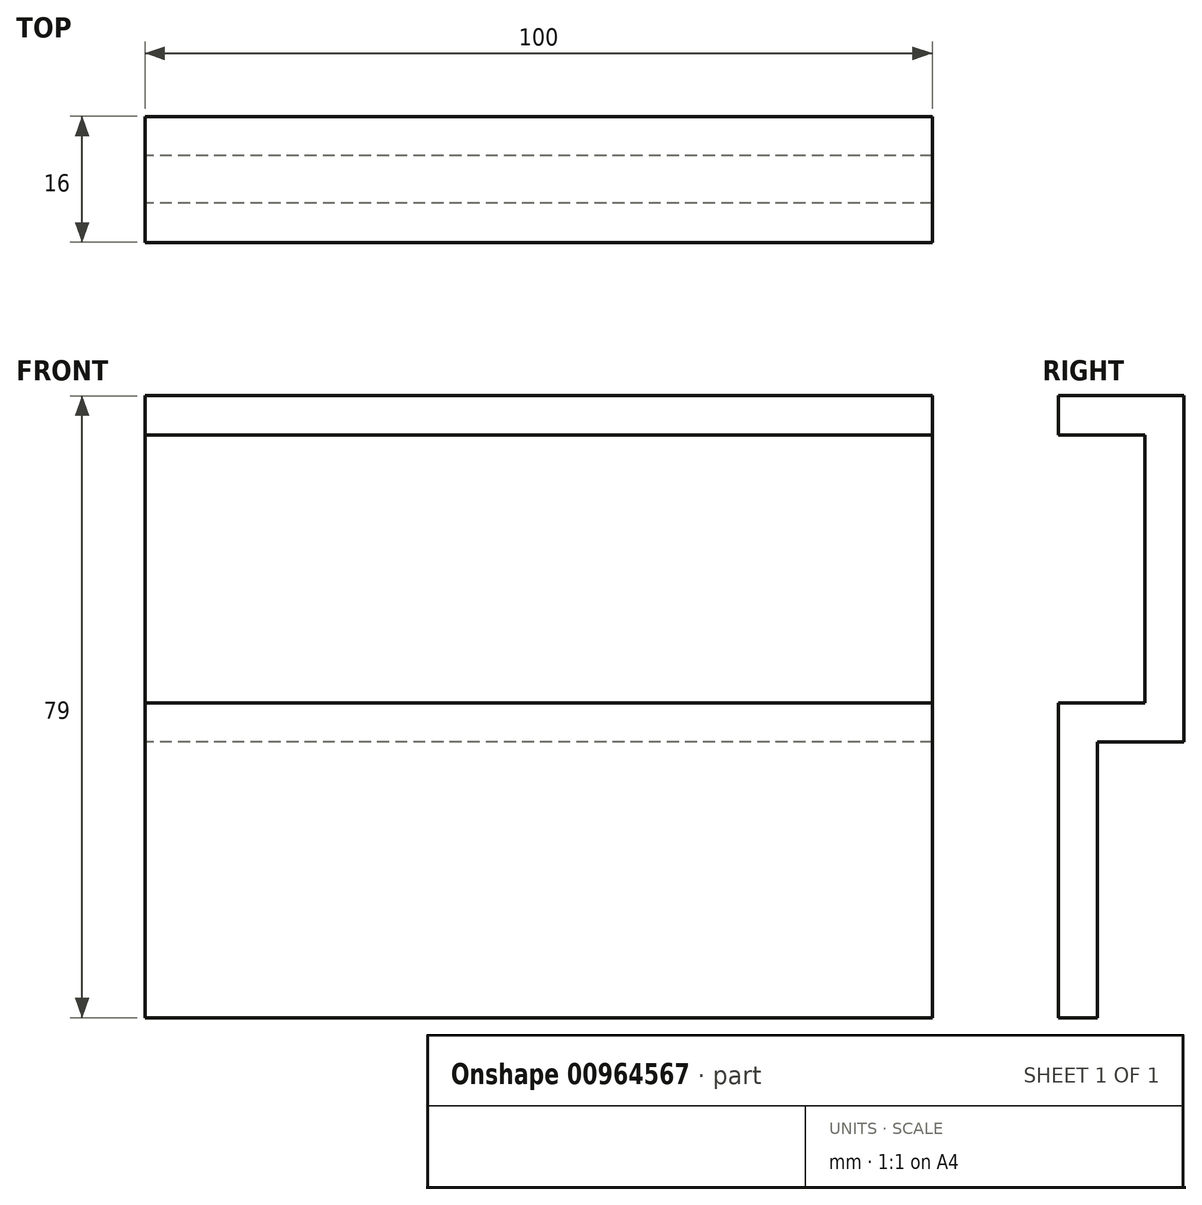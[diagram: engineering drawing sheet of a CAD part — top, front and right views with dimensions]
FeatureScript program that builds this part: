
annotation { "Feature Type Name" : "Feature", "Feature Type Description" : "" }
export const myFeature = defineFeature(function(context is Context, id is Id, definition is map)
    precondition{}
    {
        {
            var Q0;
            Q0=qCreatedBy(makeId("Right.planeOp"),FACE);
            var sketch = newSketch(context, id + "F0", { "sketchPlane" : qUnion([Q0])});
            skLineSegment(sketch, "E0", {"start": v(-10.47, 11.28) * mm, "end": v(-10.47, 6.28) * mm});
            skLineSegment(sketch, "E1", {"start": v(-10.47, 6.28) * mm, "end": v(0.53, 6.28) * mm});
            skLineSegment(sketch, "E2", {"start": v(0.53, 6.28) * mm, "end": v(0.53, -27.72) * mm});
            skLineSegment(sketch, "E3", {"start": v(0.53, -27.72) * mm, "end": v(-10.47, -27.72) * mm});
            skLineSegment(sketch, "E4", {"start": v(-10.47, -27.72) * mm, "end": v(-10.47, -67.72) * mm});
            skLineSegment(sketch, "E5", {"start": v(-10.47, -67.72) * mm, "end": v(-5.47, -67.72) * mm});
            skLineSegment(sketch, "E6", {"start": v(-5.47, -67.72) * mm, "end": v(-5.47, -32.72) * mm});
            skLineSegment(sketch, "E7", {"start": v(-5.47, -32.72) * mm, "end": v(5.53, -32.72) * mm});
            skLineSegment(sketch, "E8", {"start": v(5.53, -32.72) * mm, "end": v(5.53, 6.28) * mm});
            skLineSegment(sketch, "E9", {"start": v(5.53, 6.28) * mm, "end": v(5.53, 11.28) * mm});
            skLineSegment(sketch, "E10", {"start": v(5.53, 11.28) * mm, "end": v(-10.47, 11.28) * mm});
            skSolve(sketch);
        }
        {
            var Q0;
            Q0=makeQuery(id+"F0.imprint","IMPRINT",FACE,{"disambiguationData":[TD([[makeQuery(id+"F0.imprint","IMPRINT",EDGE,{"derivedFrom":sQuery(id+"F0.wireOp",EDGE,"E0")}),1.0]])]});
            extrude(context, id + "F1", {"entities" : qUnion([Q0]), "depth" : 100 * mm, "offsetDistance" : 25 * mm});
        }
    });
